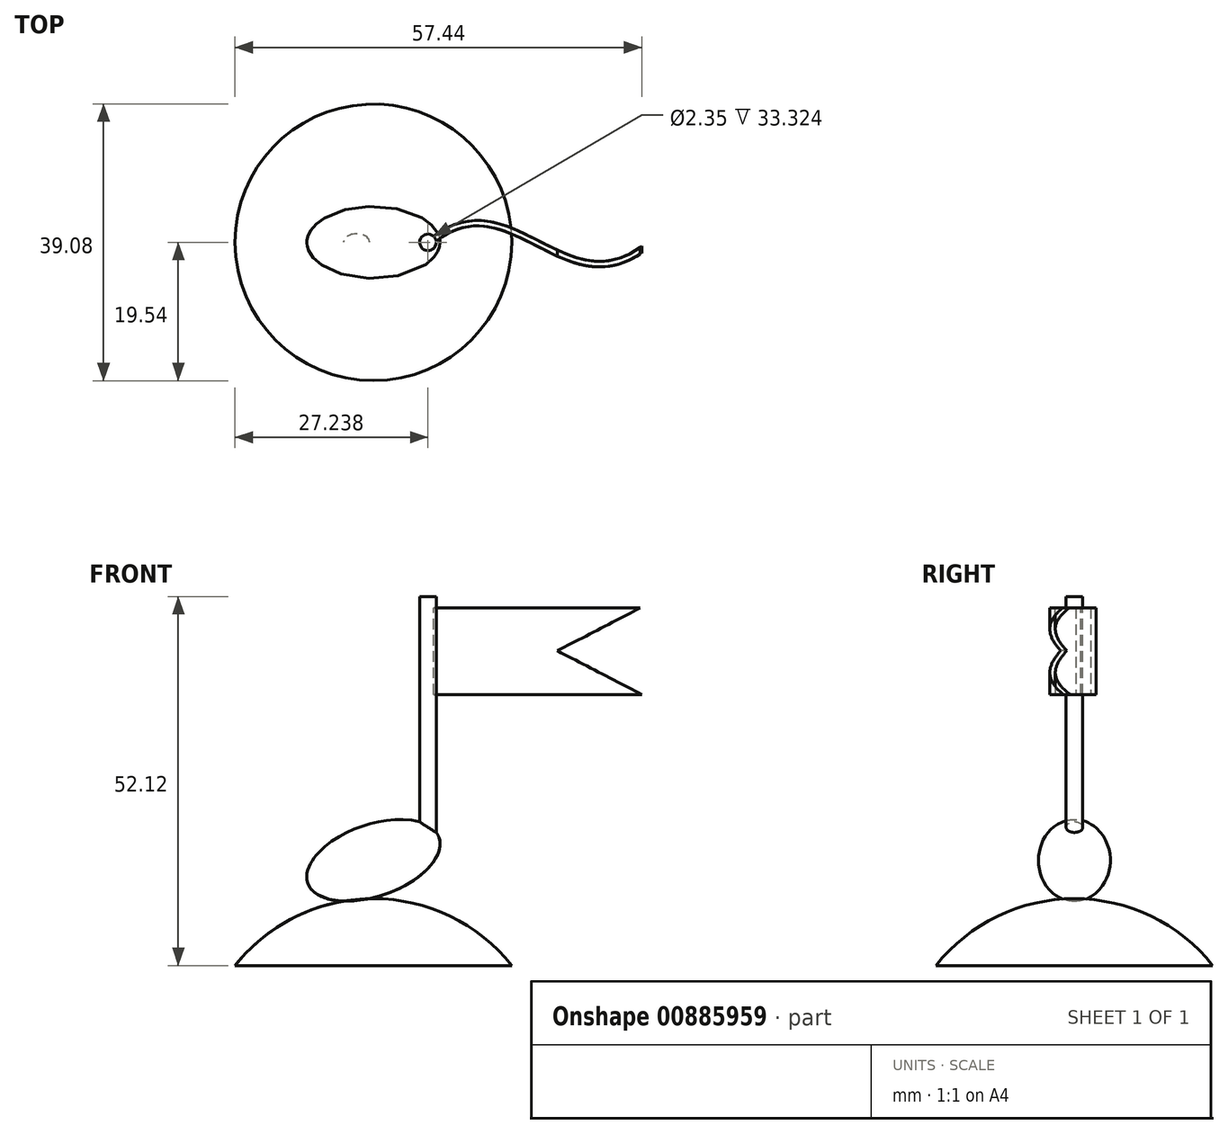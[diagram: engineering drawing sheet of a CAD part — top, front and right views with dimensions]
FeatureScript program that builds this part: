
annotation { "Feature Type Name" : "Feature", "Feature Type Description" : "" }
export const myFeature = defineFeature(function(context is Context, id is Id, definition is map)
    precondition{}
    {
        {
            var Q0;
            Q0=qCreatedBy(makeId("Front.planeOp"),FACE);
            var sketch = newSketch(context, id + "F0", { "sketchPlane" : qUnion([Q0])});
            skArc(sketch, "E0", {"start": v(0, 9.45) * mm, "mid": v(-10.85, 6.96) * mm, "end": v(-19.54, 0) * mm});
            skLineSegment(sketch, "E1", {"start": v(-19.54, 0) * mm, "end": v(0, 0) * mm});
            skLineSegment(sketch, "E2", {"start": v(0, 9.45) * mm, "end": v(0, 0) * mm});
            skSolve(sketch);
        }
        {
            var Q0;
            Q0 = qSketchRegion(id + "F0", true);
            var Q1;
            Q1=sQuery(id+"F0.wireOp",EDGE,"E2");
            revolve(context, id + "F1", {"surfaceOperationType" : NewSurfaceOperationType.NEW, "entities" : qUnion([Q0]), "axis" : qUnion([Q1]), "revolveType" : RevolveType.FULL});
        }
        {
            var Q0;
            Q0=qCreatedBy(makeId("Front.planeOp"),FACE);
            var sketch = newSketch(context, id + "F2", { "sketchPlane" : qUnion([Q0])});
            skEllipticalArc(sketch, "E3", {});
            skLineSegment(sketch, "E4", {"start": v(-9.26, 11.63) * mm, "end": v(9.26, 18.07) * mm});
            const initialGuessF2  = {"E3": [0, 0.014852266758680344, 0.9445263139852922, 0.3284357504739053, 0.009806706331106392, 0.00507515022346444, 3.141592653589793, 0]};
            skSetInitialGuess(sketch, initialGuessF2);
            skSolve(sketch);
        }
        {
            var Q0;
            Q0 = qSketchRegion(id + "F2", true);
            var Q1;
            Q1=sQuery(id+"F2.wireOp",EDGE,"E4");
            revolve(context, id + "F3", {"operationType" : NewBodyOperationType.ADD, "surfaceOperationType" : NewSurfaceOperationType.NEW, "entities" : qUnion([Q0]), "axis" : qUnion([Q1]), "revolveType" : RevolveType.FULL});
        }
        {
            var Q0;
            Q0=qCreatedBy(makeId("Front.planeOp"),FACE);
            var sketch = newSketch(context, id + "F4", { "sketchPlane" : qUnion([Q0])});
            skLineSegment(sketch, "E5.bottom", {"start": v(7.7, 52.12) * mm, "end": v(6.52, 52.12) * mm});
            skLineSegment(sketch, "E5.top", {"start": v(7.7, 17.55) * mm, "end": v(6.52, 17.55) * mm});
            skLineSegment(sketch, "E5.left", {"start": v(7.7, 52.12) * mm, "end": v(7.7, 17.55) * mm});
            skLineSegment(sketch, "E5.right", {"start": v(6.52, 52.12) * mm, "end": v(6.52, 17.55) * mm});
            skSolve(sketch);
        }
        {
            var Q0;
            Q0=qCreatedBy(makeId("Top.planeOp"),FACE);
            var sketch = newSketch(context, id + "F5", { "sketchPlane" : qUnion([Q0])});
            skFitSpline(sketch, "E6", {"points": [v(7.6, 0) * mm, v(38.79, 0) * mm], "startDerivative": vector(35.3, 30.45) * mm, "endDerivative": vector(34.72, 29.57) * mm});
            skSolve(sketch);
        }
        {
            var Q0;
            Q0 = qSketchRegion(id + "F4", true);
            var Q1;
            Q1=sQuery(id+"F4.wireOp",EDGE,"E5.left");
            revolve(context, id + "F6", {"operationType" : NewBodyOperationType.ADD, "surfaceOperationType" : NewSurfaceOperationType.NEW, "entities" : qUnion([Q0]), "axis" : qUnion([Q1]), "revolveType" : RevolveType.FULL});
        }
        {
            var Q0;
            Q0=qCreatedBy(makeId("Right.planeOp"),FACE);
            cPlane(context, id + "F7", {"entities" : qUnion([Q0]), "cplaneType" : CPlaneType.OFFSET, "offset" : 8 * mm, "width" : 150 * mm, "height" : 150 * mm});
        }
        {
            var Q0;
            Q0=qCreatedBy(id+"F7.planeOp",FACE);
            var sketch = newSketch(context, id + "F8", { "sketchPlane" : qUnion([Q0])});
            skLineSegment(sketch, "E7.bottom", {"start": v(0.5, 50.5) * mm, "end": v(-0.5, 50.5) * mm});
            skLineSegment(sketch, "E7.top", {"start": v(0.5, 38.3) * mm, "end": v(-0.5, 38.3) * mm});
            skLineSegment(sketch, "E7.left", {"start": v(0.5, 50.5) * mm, "end": v(0.5, 38.3) * mm});
            skLineSegment(sketch, "E7.right", {"start": v(-0.5, 50.5) * mm, "end": v(-0.5, 38.3) * mm});
            skPoint(sketch, "E7.middle", {"position": v(0, 44.4) * mm});
            skSolve(sketch);
        }
        {
            var Q0;
            Q0 = qSketchRegion(id + "F8", true);
            var Q1;
            Q1=sQuery(id+"F5.wireOp",EDGE,"E6");
            sweep(context, id + "F9", {"operationType" : NewBodyOperationType.ADD, "profiles" : qUnion([Q0]), "path" : qUnion([Q1])});
        }
        {
            var Q0;
            Q0=qCreatedBy(makeId("Front.planeOp"),FACE);
            var sketch = newSketch(context, id + "F10", { "sketchPlane" : qUnion([Q0])});
            skLineSegment(sketch, "E8", {"start": v(40.06, 51.75) * mm, "end": v(25.97, 44.46) * mm});
            skLineSegment(sketch, "E9", {"start": v(25.97, 44.46) * mm, "end": v(40.06, 37.18) * mm});
            skLineSegment(sketch, "E10", {"start": v(40.06, 37.18) * mm, "end": v(40.06, 51.75) * mm});
            skSolve(sketch);
        }
        {
            var Q0;
            Q0 = qSketchRegion(id + "F10", true);
            var Q1;
            Q1=sQuery(id+"F10.wireOp",EDGE,"E8");
            var Q2;
            Q2=sQuery(id+"F10.wireOp",EDGE,"E10");
            var Q3;
            Q3=sQuery(id+"F10.wireOp",EDGE,"E9");
            extrude(context, id + "F11", {"entities" : qUnion([Q0]), "operationType" : NewBodyOperationType.REMOVE, "surfaceEntities" : qUnion([Q1, Q2, Q3]), "endBound" : BoundingType.THROUGH_ALL, "oppositeDirection" : true, "depth" : 25 * mm, "offsetDistance" : 25 * mm, "hasSecondDirection" : true, "secondDirectionBound" : SecondDirectionBoundingType.THROUGH_ALL, "secondDirectionOppositeDirection" : false, "secondDirectionDepth" : 25 * mm});
        }
    });
